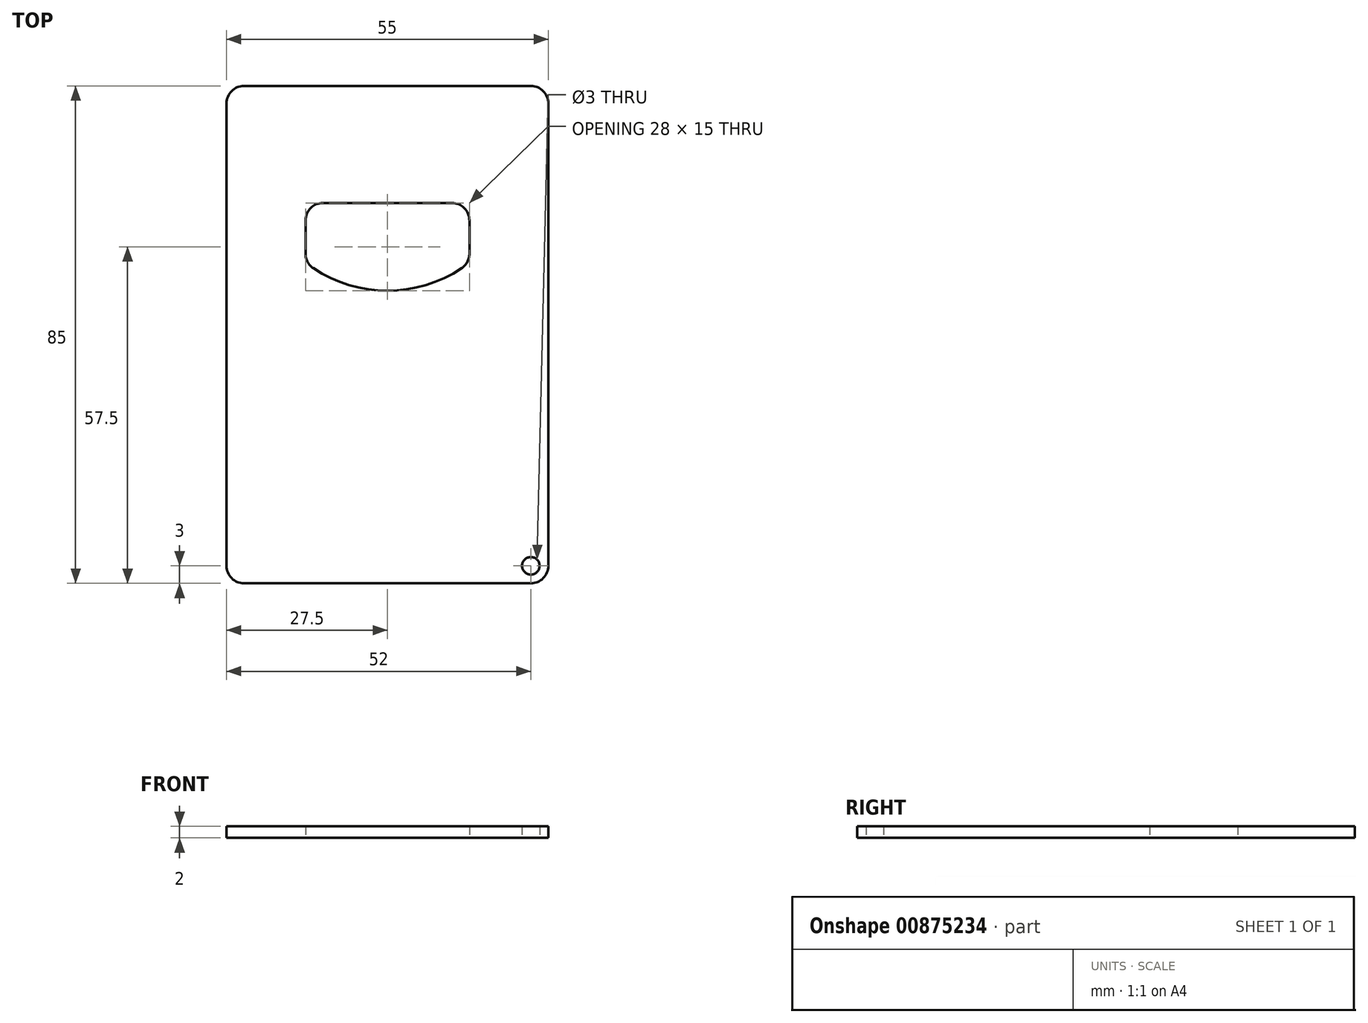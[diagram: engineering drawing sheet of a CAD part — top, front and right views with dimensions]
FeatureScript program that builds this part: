
annotation { "Feature Type Name" : "Feature", "Feature Type Description" : "" }
export const myFeature = defineFeature(function(context is Context, id is Id, definition is map)
    precondition{}
    {
        {
            var Q0;
            Q0=qCreatedBy(makeId("Top.planeOp"),FACE);
            var sketch = newSketch(context, id + "F0", { "sketchPlane" : qUnion([Q0])});
            skLineSegment(sketch, "E0.bottom", {"start": v(24.5, 42.5) * mm, "end": v(-24.5, 42.5) * mm});
            skLineSegment(sketch, "E0.top", {"start": v(24.5, -42.5) * mm, "end": v(-24.5, -42.5) * mm});
            skLineSegment(sketch, "E0.left", {"start": v(27.5, 39.5) * mm, "end": v(27.5, -39.5) * mm});
            skLineSegment(sketch, "E0.right", {"start": v(-27.5, 39.5) * mm, "end": v(-27.5, -39.5) * mm});
            skPoint(sketch, "E0.middle", {"position": v(0, 0) * mm});
            skLineSegment(sketch, "E1", {"start": v(0, -42.5) * mm, "end": v(0, 7.5) * mm, "construction": true});
            skPoint(sketch, "E2.visualSharp", {"position": v(-27.5, 42.5) * mm});
            skArc(sketch, "E2.filletArc", {"start": v(-24.5, 42.5) * mm, "mid": v(-26.62, 41.62) * mm, "end": v(-27.5, 39.5) * mm});
            skPoint(sketch, "E3.visualSharp", {"position": v(27.5, 42.5) * mm});
            skArc(sketch, "E3.filletArc", {"start": v(27.5, 39.5) * mm, "mid": v(26.62, 41.62) * mm, "end": v(24.5, 42.5) * mm});
            skPoint(sketch, "E4.visualSharp", {"position": v(27.5, -42.5) * mm});
            skArc(sketch, "E4.filletArc", {"start": v(24.5, -42.5) * mm, "mid": v(26.62, -41.62) * mm, "end": v(27.5, -39.5) * mm});
            skPoint(sketch, "E5.visualSharp", {"position": v(-27.5, -42.5) * mm});
            skArc(sketch, "E5.filletArc", {"start": v(-27.5, -39.5) * mm, "mid": v(-26.62, -41.62) * mm, "end": v(-24.5, -42.5) * mm});
            skLineSegment(sketch, "E6", {"start": v(14, 13.83) * mm, "end": v(14, 19.5) * mm});
            skLineSegment(sketch, "E7", {"start": v(11, 22.5) * mm, "end": v(0, 22.5) * mm});
            skArc(sketch, "E8", {"start": v(0, 7.5) * mm, "mid": v(6.62, 8.48) * mm, "end": v(12.67, 11.34) * mm});
            skPoint(sketch, "E9.orphan", {"position": v(14, 7.5) * mm});
            skLineSegment(sketch, "E10.MirrorCS", {"start": v(-11, 22.5) * mm, "end": v(0, 22.5) * mm});
            skLineSegment(sketch, "E11.MirrorCS", {"start": v(-14, 13.83) * mm, "end": v(-14, 19.5) * mm});
            skArc(sketch, "E12.MirrorCS", {"start": v(0, 7.5) * mm, "mid": v(-6.62, 8.48) * mm, "end": v(-12.67, 11.34) * mm});
            skPoint(sketch, "E13.visualSharp", {"position": v(-14, 22.5) * mm});
            skArc(sketch, "E13.filletArc", {"start": v(-11, 22.5) * mm, "mid": v(-13.12, 21.62) * mm, "end": v(-14, 19.5) * mm});
            skPoint(sketch, "E14.visualSharp", {"position": v(14, 22.5) * mm});
            skArc(sketch, "E14.filletArc", {"start": v(14, 19.5) * mm, "mid": v(13.12, 21.62) * mm, "end": v(11, 22.5) * mm});
            skPoint(sketch, "E15.visualSharp", {"position": v(14, 12.3) * mm});
            skArc(sketch, "E15.filletArc", {"start": v(12.67, 11.34) * mm, "mid": v(13.65, 12.42) * mm, "end": v(14, 13.83) * mm});
            skPoint(sketch, "E16.visualSharp", {"position": v(-14, 12.3) * mm});
            skArc(sketch, "E16.filletArc", {"start": v(-14, 13.83) * mm, "mid": v(-13.65, 12.42) * mm, "end": v(-12.67, 11.34) * mm});
            skCircle(sketch, "E17", {"center": v(24.5, -39.5) * mm, "radius": 1.5 * mm});
            skSolve(sketch);
        }
        {
            var Q0;
            Q0=makeQuery(id+"F0.imprint","IMPRINT",FACE,{"disambiguationData":[TD([[makeQuery(id+"F0.imprint","IMPRINT",EDGE,{"derivedFrom":sQuery(id+"F0.wireOp",EDGE,"E0.bottom")}),1.0]])]});
            extrude(context, id + "F1", {"entities" : qUnion([Q0]), "depth" : 2 * mm, "offsetDistance" : 25 * mm});
        }
    });
